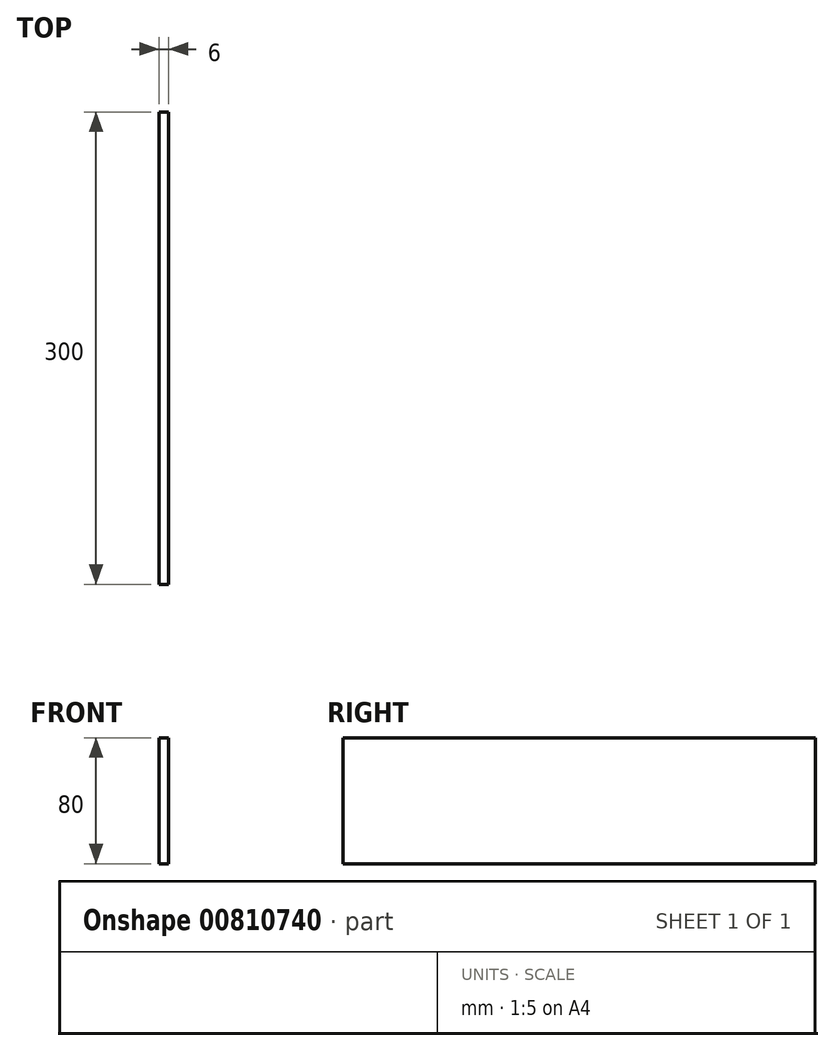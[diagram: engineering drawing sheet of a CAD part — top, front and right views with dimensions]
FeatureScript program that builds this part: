
annotation { "Feature Type Name" : "Feature", "Feature Type Description" : "" }
export const myFeature = defineFeature(function(context is Context, id is Id, definition is map)
    precondition{}
    {
        {
            var Q0;
            Q0=qCreatedBy(makeId("Top.planeOp"),FACE);
            var sketch = newSketch(context, id + "F0", { "sketchPlane" : qUnion([Q0])});
            skLineSegment(sketch, "E0.bottom", {"start": v(3, -150) * mm, "end": v(-3, -150) * mm});
            skLineSegment(sketch, "E0.top", {"start": v(3, 150) * mm, "end": v(-3, 150) * mm});
            skLineSegment(sketch, "E0.left", {"start": v(3, -150) * mm, "end": v(3, 150) * mm});
            skLineSegment(sketch, "E0.right", {"start": v(-3, -150) * mm, "end": v(-3, 150) * mm});
            skPoint(sketch, "E0.middle", {"position": v(0, 0) * mm});
            skSolve(sketch);
        }
        {
            var Q0;
            Q0 = qSketchRegion(id + "F0", true);
            extrude(context, id + "F1", {"entities" : qUnion([Q0]), "depth" : 80 * mm, "offsetDistance" : 25 * mm});
        }
    });
